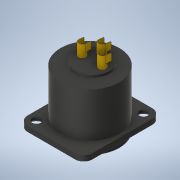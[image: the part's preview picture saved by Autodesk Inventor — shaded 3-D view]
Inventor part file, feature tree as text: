
AUTODESK INVENTOR PART (.ipt)
format: ipt  version: 2020.1 (Build 241239000, 239)  size: 1,618,944 bytes
history: native  units: mm
features: other x12, surface_op x7, sketch x4, extrude x1
ambient origin geometry x8: Origin, YZ Plane, XZ Plane, XY Plane, X Axis, Y Axis, Z Axis, Center Point
bodies: Solid1 (feature_tree), Solid2 (feature_tree), Solid3 (feature_tree), Solid4 (feature_tree), Solid5 (feature_tree)
feature tree (24):
  surface_op  "Sculpt1"
  extrude  "Extrusion1"  TaperAngle=0.0deg  [1 undecoded]
  sketch  "Sketch2"  dims[d2=5.0mm]
  sketch  "Sketch3"  dims[d3=0.0mm]
  sketch  "Sketch4"  dims[d4=5.0mm d5=0.0mm d6=5.0mm d7=0.0mm d8=5.0mm d9=0.0mm d10=5.0mm d11=0.0mm d12=25.4mm d13=0.0mm d14=2.54mm]
  other  "Srf3"
  other  "Srf4"
  other  "Srf5"
  other  "Srf6"
  other  "Srf7"
  other  "Srf8"
  sketch  "Sketch1"  dims[d0=5.0mm d1=0.0mm]
  other  "push button"
  other  "brep_2"
  other  "brep_3"
  other  "brep_4"
  other  "Composite1"
  other  "Srf1"
  surface_op  "Boundary Patch1"
  surface_op  "Boundary Patch2"
  surface_op  "Boundary Patch3"
  surface_op  "Boundary Patch4"
  surface_op  "Boundary Patch5"
  surface_op  "Boundary Patch6"
note: 1 required parameter value undecoded (feature->parameter linkage not recoverable at this tier; creation-order binding heuristic only, values carry confidence <= 0.55)
